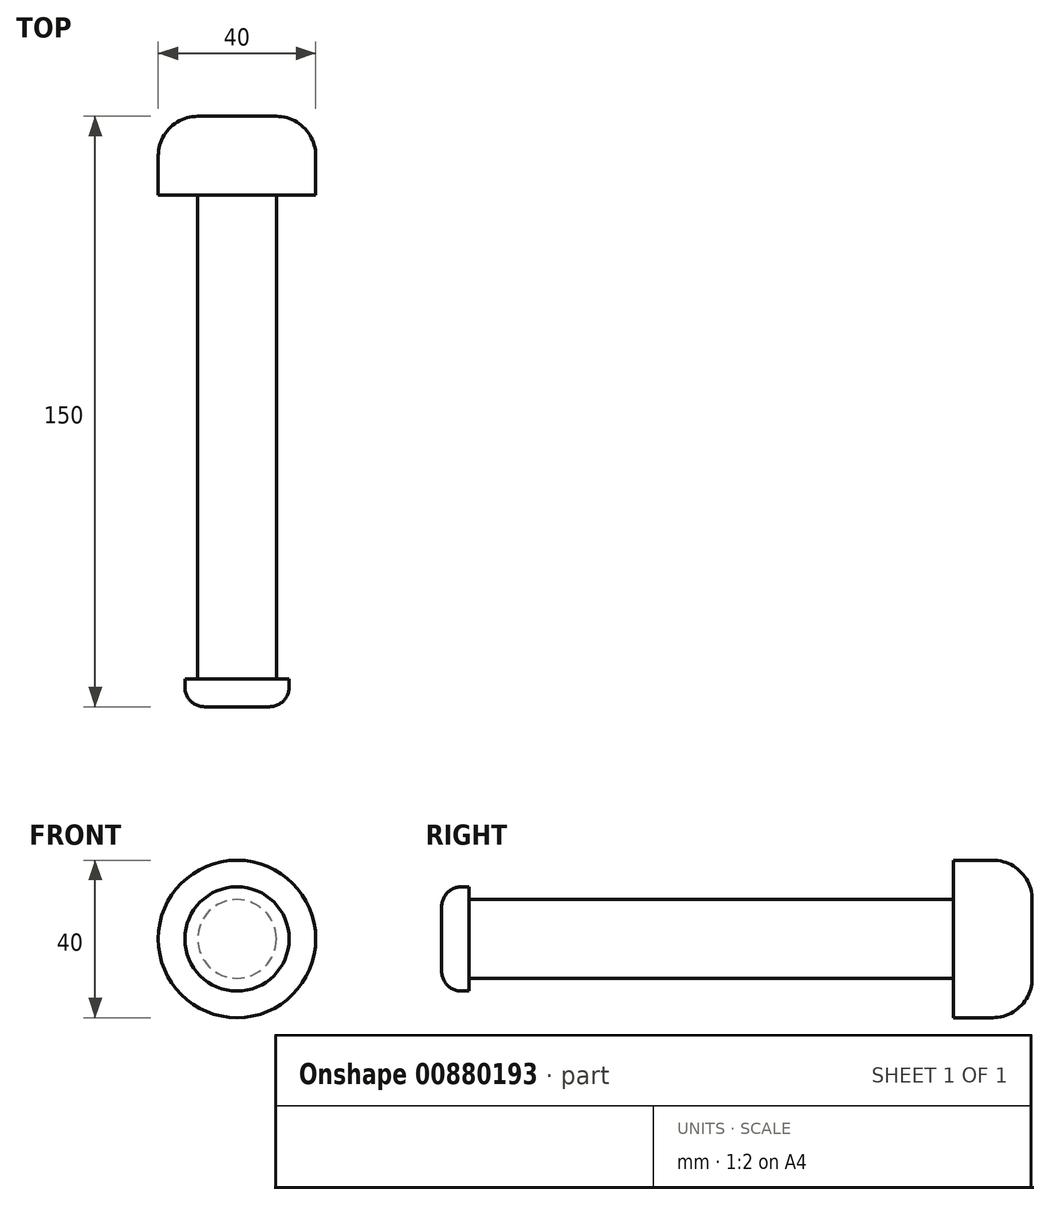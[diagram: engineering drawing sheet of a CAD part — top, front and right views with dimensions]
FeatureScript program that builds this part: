
annotation { "Feature Type Name" : "Feature", "Feature Type Description" : "" }
export const myFeature = defineFeature(function(context is Context, id is Id, definition is map)
    precondition{}
    {
        {
            var Q0;
            Q0=qCreatedBy(makeId("Front.planeOp"),FACE);
            var sketch = newSketch(context, id + "F0", { "sketchPlane" : qUnion([Q0])});
            skCircle(sketch, "E0", {"center": v(-0.8, 2.69) * mm, "radius": 10 * mm});
            skSolve(sketch);
        }
        {
            var Q0;
            Q0 = qSketchRegion(id + "F0", true);
            extrude(context, id + "F1", {"entities" : qUnion([Q0]), "depth" : 130 * mm, "offsetDistance" : 25 * mm});
        }
        {
            var Q0;
            Q0=makeQuery(id+"F1.opExtrude","CAP_FACE",FACE,{"disambiguationData":[OSD([sQuery(id+"F0.wireOp",EDGE,"E0")])],"isStart":true});
            var sketch = newSketch(context, id + "F2", { "sketchPlane" : qUnion([Q0])});
            skCircle(sketch, "E1", {"center": v(0.8, 2.69) * mm, "radius": 20 * mm});
            skSolve(sketch);
        }
        {
            var Q0;
            Q0 = qSketchRegion(id + "F2", true);
            extrude(context, id + "F3", {"entities" : qUnion([Q0]), "operationType" : NewBodyOperationType.ADD, "depth" : 20 * mm, "offsetDistance" : 25 * mm});
        }
        {
            var Q0;
            Q0=makeQuery(id+"F3.opExtrude","CAP_EDGE",EDGE,{"disambiguationData":[OSD([sQuery(id+"F2.wireOp",EDGE,"E1")])],"isStart":false});
            fillet(context, id + "F4", {"entities" : qUnion([Q0]), "radius" : 10 * mm, "tangentPropagation" : true, "allowEdgeOverflow" : false});
        }
        {
            var Q0;
            Q0=makeQuery(id+"F1.opExtrude","CAP_FACE",FACE,{"disambiguationData":[OSD([sQuery(id+"F0.wireOp",EDGE,"E0")])],"isStart":false});
            var sketch = newSketch(context, id + "F5", { "sketchPlane" : qUnion([Q0])});
            skCircle(sketch, "E2", {"center": v(-0.8, 2.69) * mm, "radius": 13.24 * mm});
            skSolve(sketch);
        }
        {
            var Q0;
            Q0 = qSketchRegion(id + "F5", true);
            extrude(context, id + "F6", {"entities" : qUnion([Q0]), "operationType" : NewBodyOperationType.ADD, "oppositeDirection" : true, "depth" : 7 * mm, "offsetDistance" : 25 * mm});
        }
        {
            var Q0;
            Q0=makeQuery(id+"F6.opExtrude","CAP_EDGE",EDGE,{"disambiguationData":[OSD([sQuery(id+"F5.wireOp",EDGE,"E2")])],"isStart":true});
            fillet(context, id + "F7", {"entities" : qUnion([Q0]), "radius" : 5 * mm, "tangentPropagation" : true, "allowEdgeOverflow" : false});
        }
    });
